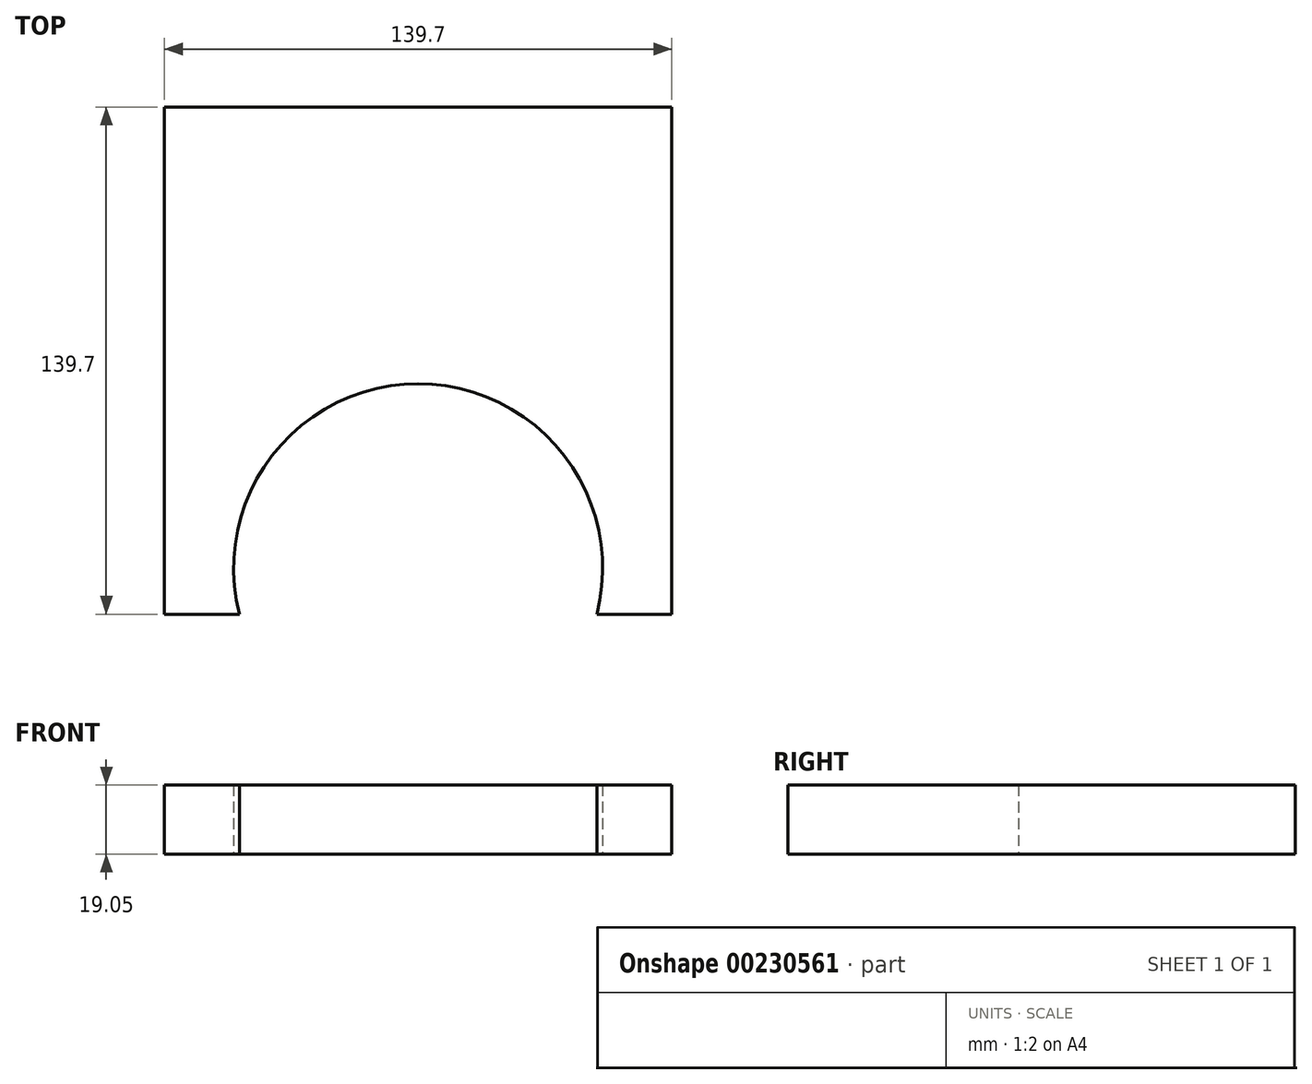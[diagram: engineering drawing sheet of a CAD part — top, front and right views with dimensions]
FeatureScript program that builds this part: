
annotation { "Feature Type Name" : "Feature", "Feature Type Description" : "" }
export const myFeature = defineFeature(function(context is Context, id is Id, definition is map)
    precondition{}
    {
        {
            var Q0;
            Q0=qCreatedBy(makeId("Top.planeOp"),FACE);
            var sketch = newSketch(context, id + "F0", { "sketchPlane" : qUnion([Q0])});
            skLineSegment(sketch, "E0.bottom", {"start": v(-69.85, 69.85) * mm, "end": v(69.85, 69.85) * mm});
            skLineSegment(sketch, "E0.top", {"start": v(-69.85, -69.85) * mm, "end": v(-49.19, -69.85) * mm});
            skLineSegment(sketch, "E0.left", {"start": v(-69.85, 69.85) * mm, "end": v(-69.85, -69.85) * mm});
            skLineSegment(sketch, "E0.right", {"start": v(69.85, 69.85) * mm, "end": v(69.85, -69.85) * mm});
            skPoint(sketch, "E0.middle", {"position": v(0, 0) * mm});
            skLineSegment(sketch, "E1", {"start": v(0, -69.85) * mm, "end": v(0, -57.15) * mm});
            skPoint(sketch, "E1.endSnap0", {"position": v(0, -69.85) * mm});
            skArc(sketch, "E2", {"start": v(49.19, -69.85) * mm, "mid": v(0, -6.35) * mm, "end": v(-49.19, -69.85) * mm});
            skLineSegment(sketch, "E3.trimOffspring", {"start": v(49.19, -69.85) * mm, "end": v(69.85, -69.85) * mm});
            skSolve(sketch);
        }
        {
            var Q0;
            Q0=makeQuery(id+"F0.imprint","IMPRINT",FACE,{"disambiguationData":[TD([[makeQuery(id+"F0.imprint","IMPRINT",EDGE,{"derivedFrom":sQuery(id+"F0.wireOp",EDGE,"E0.bottom")}),-1.0]])]});
            extrude(context, id + "F1", {"entities" : qUnion([Q0]), "depth" : 19.05 * mm});
        }
    });
